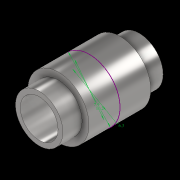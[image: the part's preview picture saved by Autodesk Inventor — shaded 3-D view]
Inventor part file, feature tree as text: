
AUTODESK INVENTOR PART (.ipt)
format: ipt  version: 2022.2 (Build 262287010, 287A)  size: 153,600 bytes
history: native  units: mm
features: extrude x2, sketch x1
ambient origin geometry x8: Origin, YZ Plane, XZ Plane, XY Plane, X Axis, Y Axis, Z Axis, Center Point
bodies: Solid1 (feature_tree)
feature tree (3):
  sketch  "Sketch1"  dims[d0=10.2mm d1=7.9mm d2=10.3mm d3=0.0mm d4=6.3mm d5=16.7mm d6=0.0mm]
  extrude  "Extrusion1"  Depth=16.7mm
  extrude  "Extrusion2"  Depth=10.3mm TaperAngle=0.0deg
